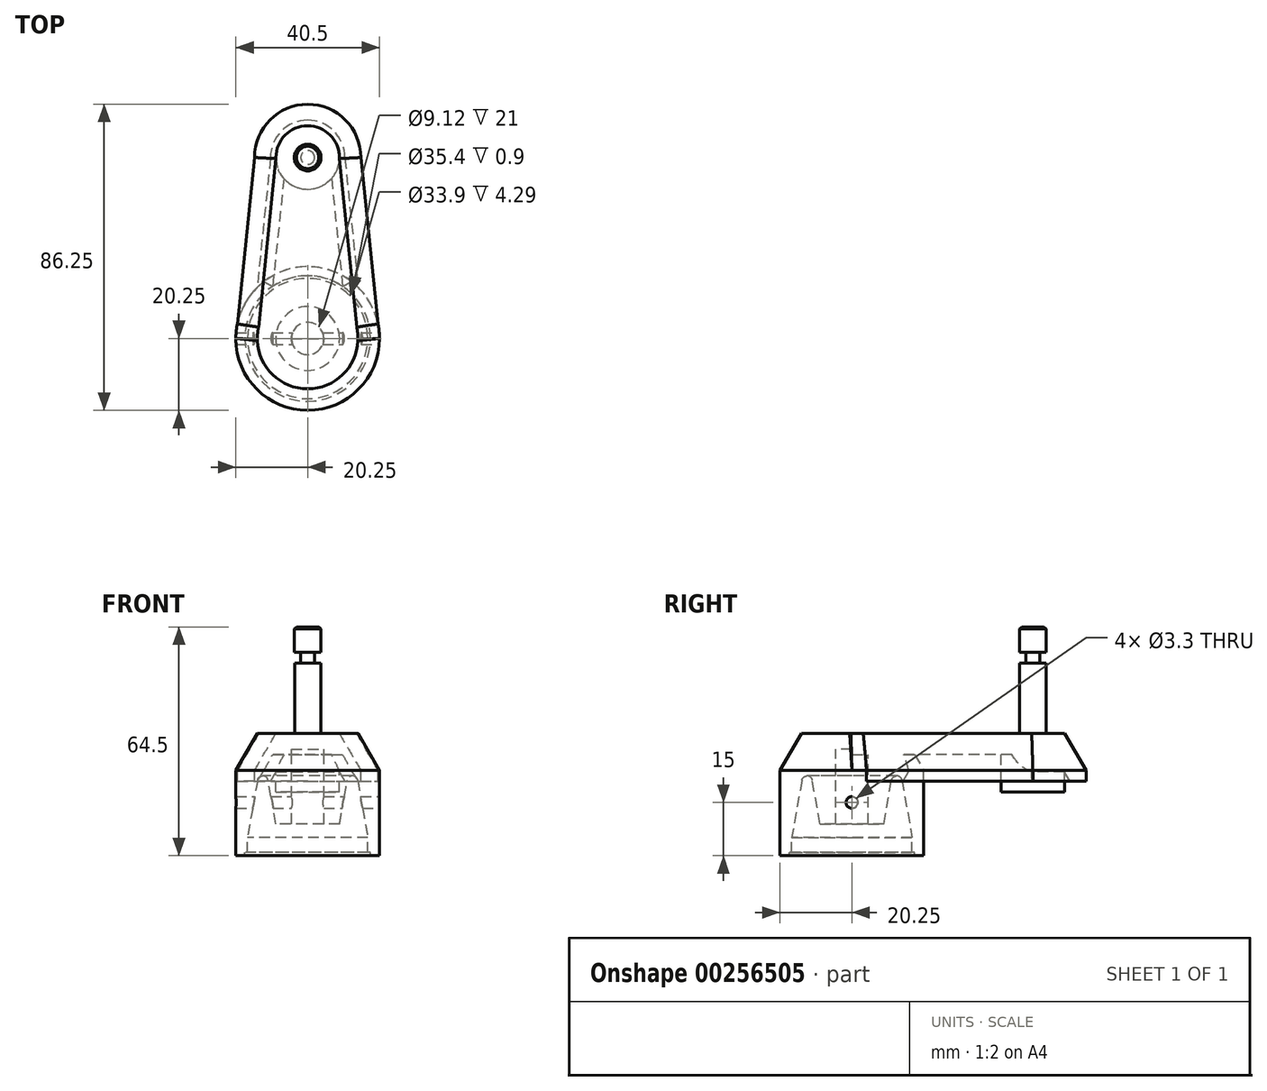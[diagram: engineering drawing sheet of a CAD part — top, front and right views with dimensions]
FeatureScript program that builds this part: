
annotation { "Feature Type Name" : "Feature", "Feature Type Description" : "" }
export const myFeature = defineFeature(function(context is Context, id is Id, definition is map)
    precondition{}
    {
        {
            var Q0;
            Q0=qCreatedBy(makeId("Right.planeOp"),FACE);
            var sketch = newSketch(context, id + "F0", { "sketchPlane" : qUnion([Q0])});
            skPoint(sketch, "E0", {"position": v(0, 11.5) * mm});
            skPoint(sketch, "E1", {"position": v(0, 10) * mm});
            skLineSegment(sketch, "E2", {"start": v(0, 10) * mm, "end": v(-1.52, 10) * mm});
            skLineSegment(sketch, "E3", {"start": v(-1.52, 10) * mm, "end": v(-1.52, 3) * mm});
            skLineSegment(sketch, "E4", {"start": v(-1.52, 3) * mm, "end": v(-3, 3) * mm});
            skLineSegment(sketch, "E5", {"start": v(-3, 3) * mm, "end": v(-3.72, 7.09) * mm});
            skLineSegment(sketch, "E6", {"start": v(-4.7, 7.09) * mm, "end": v(-5.65, 1.73) * mm});
            skLineSegment(sketch, "E7", {"start": v(-5.65, 1.73) * mm, "end": v(-5.65, 0.3) * mm});
            skLineSegment(sketch, "E8", {"start": v(-5.65, 0.3) * mm, "end": v(-5.9, 0.3) * mm});
            skLineSegment(sketch, "E9", {"start": v(-5.9, 0.3) * mm, "end": v(-5.9, 0) * mm});
            skLineSegment(sketch, "E10", {"start": v(-5.9, 0) * mm, "end": v(-6.75, 0) * mm});
            skLineSegment(sketch, "E11", {"start": v(-6.75, 0) * mm, "end": v(-6.75, 8) * mm});
            skLineSegment(sketch, "E12", {"start": v(-6.75, 8) * mm, "end": v(-4.73, 11.5) * mm});
            skLineSegment(sketch, "E13", {"start": v(-4.73, 11.5) * mm, "end": v(0, 11.5) * mm});
            skLineSegment(sketch, "E14", {"start": v(-5.65, 1.73) * mm, "end": v(-5.65, 11.5) * mm, "construction": true});
            skLineSegment(sketch, "E15", {"start": v(-3, 3) * mm, "end": v(-3, 11.5) * mm, "construction": true});
            skPoint(sketch, "E16.visualSharp", {"position": v(-4.21, 9.88) * mm});
            skArc(sketch, "E16.filletArc", {"start": v(-3.72, 7.09) * mm, "mid": v(-4.21, 7.5) * mm, "end": v(-4.7, 7.09) * mm});
            skLineSegment(sketch, "E17", {"start": v(-6.75, 8) * mm, "end": v(-6.75, 11.5) * mm, "construction": true});
            skLineSegment(sketch, "E18", {"start": v(0, 11.5) * mm, "end": v(0, 10) * mm});
            skSolve(sketch);
        }
        {
            var Q0;
            Q0=makeQuery(id+"F0.imprint","IMPRINT",FACE,{"disambiguationData":[TD([[makeQuery(id+"F0.imprint","IMPRINT",EDGE,{"derivedFrom":sQuery(id+"F0.wireOp",EDGE,"E2")}),-1.0]])]});
            var Q1;
            Q1=sQuery(id+"F0.wireOp",EDGE,"E18");
            revolve(context, id + "F1", {"entities" : qUnion([Q0]), "axis" : qUnion([Q1]), "revolveType" : RevolveType.FULL});
        }
        {
            var Q0;
            Q0=qCreatedBy(makeId("Right.planeOp"),FACE);
            var sketch = newSketch(context, id + "F2", { "sketchPlane" : qUnion([Q0])});
            skLineSegment(sketch, "E19", {"start": v(0, 0) * mm, "end": v(17, 0) * mm, "construction": true});
            skLineSegment(sketch, "E20", {"start": v(17, 0) * mm, "end": v(17, 11.5) * mm, "construction": true});
            skPoint(sketch, "E21", {"position": v(17, 9.5) * mm});
            skLineSegment(sketch, "E22", {"start": v(20.5, 7) * mm, "end": v(22, 7) * mm});
            skLineSegment(sketch, "E23", {"start": v(22, 7) * mm, "end": v(22, 8) * mm});
            skLineSegment(sketch, "E24", {"start": v(22, 8) * mm, "end": v(19.98, 11.5) * mm});
            skLineSegment(sketch, "E25", {"start": v(19.98, 11.5) * mm, "end": v(17, 11.5) * mm});
            skLineSegment(sketch, "E26", {"start": v(17, 9.5) * mm, "end": v(17, 11.5) * mm});
            skLineSegment(sketch, "E27", {"start": v(20.5, 7) * mm, "end": v(20.5, 0) * mm, "construction": true});
            skLineSegment(sketch, "E28", {"start": v(20.5, 7) * mm, "end": v(19.06, 9.5) * mm});
            skLineSegment(sketch, "E29", {"start": v(19.06, 9.5) * mm, "end": v(17, 9.5) * mm});
            skSolve(sketch);
        }
        {
            var Q0;
            Q0=qCreatedBy(makeId("Top.planeOp"),FACE);
            cPlane(context, id + "F3", {"entities" : qUnion([Q0]), "cplaneType" : CPlaneType.OFFSET, "offset" : 8 * mm, "width" : 150 * mm, "height" : 150 * mm});
        }
        {
            var Q0;
            Q0=qCreatedBy(id+"F3.planeOp",FACE);
            var sketch = newSketch(context, id + "F4", { "sketchPlane" : qUnion([Q0])});
            skArc(sketch, "E30", {"start": v(5, 17) * mm, "mid": v(3.54, 20.54) * mm, "end": v(0, 22) * mm});
            skPoint(sketch, "E31", {"position": v(0, 0) * mm});
            skLineSegment(sketch, "E32", {"start": v(-5, 17) * mm, "end": v(-6.75, 0) * mm});
            skLineSegment(sketch, "E33", {"start": v(5, 17) * mm, "end": v(6.75, 0) * mm});
            skLineSegment(sketch, "E34", {"start": v(0, 17) * mm, "end": v(0, 22) * mm, "construction": true});
            skLineSegment(sketch, "E35", {"start": v(0, 22) * mm, "end": v(0, 17) * mm, "construction": true});
            skArc(sketch, "E36", {"start": v(0, 22) * mm, "mid": v(-3.54, 20.54) * mm, "end": v(-5, 17) * mm});
            skSolve(sketch);
        }
        {
            var Q0;
            Q0=makeQuery(id+"F2.imprint","IMPRINT",FACE,{"disambiguationData":[TD([[makeQuery(id+"F2.imprint","IMPRINT",EDGE,{"derivedFrom":sQuery(id+"F2.wireOp",EDGE,"E22")}),1.0]])]});
            var Q1;
            Q1=sQuery(id+"F4.wireOp",EDGE,"E30");
            var Q2;
            Q2=sQuery(id+"F4.wireOp",EDGE,"E33");
            sweep(context, id + "F5", {"operationType" : NewBodyOperationType.ADD, "profiles" : qUnion([Q0]), "path" : qUnion([Q1, Q2])});
        }
        {
            var Q0;
            Q0=makeQuery(id+"F2.imprint","IMPRINT",FACE,{"disambiguationData":[TD([[makeQuery(id+"F2.imprint","IMPRINT",EDGE,{"derivedFrom":sQuery(id+"F2.wireOp",EDGE,"E22")}),1.0]])]});
            var Q1;
            Q1=sQuery(id+"F4.wireOp",EDGE,"E36");
            var Q2;
            Q2=sQuery(id+"F4.wireOp",EDGE,"E32");
            sweep(context, id + "F6", {"operationType" : NewBodyOperationType.ADD, "profiles" : qUnion([Q0]), "path" : qUnion([Q1, Q2])});
        }
        {
            var Q0;
            Q0=qCreatedBy(makeId("Front.planeOp"),FACE);
            var sketch = newSketch(context, id + "F7", { "sketchPlane" : qUnion([Q0])});
            skLineSegment(sketch, "E37.bottom", {"start": v(-2.5, 11.5) * mm, "end": v(2.5, 11.5) * mm});
            skLineSegment(sketch, "E37.top", {"start": v(-2.5, 9.5) * mm, "end": v(2.5, 9.5) * mm});
            skLineSegment(sketch, "E37.left", {"start": v(-2.5, 11.5) * mm, "end": v(-2.5, 9.5) * mm});
            skLineSegment(sketch, "E37.right", {"start": v(2.5, 11.5) * mm, "end": v(2.5, 9.5) * mm});
            skSolve(sketch);
        }
        {
            var Q0;
            Q0=makeQuery(id+"F7.imprint","IMPRINT",FACE,{"disambiguationData":[TD([[makeQuery(id+"F7.imprint","IMPRINT",EDGE,{"derivedFrom":sQuery(id+"F7.wireOp",EDGE,"E37.bottom")}),-1.0]])]});
            extrude(context, id + "F8", {"entities" : qUnion([Q0]), "operationType" : NewBodyOperationType.ADD, "oppositeDirection" : true, "depth" : 17 * mm});
        }
        {
            var Q0;
            {var subQ0=sQuery(id+"F2.wireOp",EDGE,"E25");Q0=makeQuery(id+"F8.boolean.opBoolean","MERGE",FACE,{"derivedFrom":[makeQuery(id+"F6.boolean.opBoolean","MERGE",FACE,{"derivedFrom":[makeQuery(id+"F5.boolean.opBoolean","MERGE",FACE,{"derivedFrom":[makeQuery(id+"F1.opRevolve","SWEPT_FACE",FACE,{"disambiguationData":[OSD([sQuery(id+"F0.wireOp",EDGE,"E13")])]}),makeQuery(id+"F5.opSweep","MID_CAP_FACE",FACE,{"disambiguationData":[OSD([subQ0,sQuery(id+"F4.wireOp",VERTEX,"E33.start")])],"capPos":1.0})]}),makeQuery(id+"F6.opSweep","MID_CAP_FACE",FACE,{"disambiguationData":[OSD([subQ0,sQuery(id+"F4.wireOp",VERTEX,"E32.start")])],"capPos":1.0})]}),makeQuery(id+"F8.opExtrude","SWEPT_FACE",FACE,{"disambiguationData":[OSD([sQuery(id+"F7.wireOp",EDGE,"E37.bottom")])]})]});}
            var sketch = newSketch(context, id + "F9", { "sketchPlane" : qUnion([Q0])});
            skLineSegment(sketch, "E38", {"start": v(0, 0) * mm, "end": v(0, 17) * mm, "construction": true});
            skCircle(sketch, "E39", {"center": v(0, 17) * mm, "radius": 2.98 * mm});
            skCircle(sketch, "E40", {"center": v(0, 17) * mm, "radius": 1.23 * mm});
            skSolve(sketch);
        }
        {
            var Q0;
            {var subQ0=sQuery(id+"F2.wireOp",EDGE,"E24");var subQ1=sQuery(id+"F2.wireOp",EDGE,"E25");var subQ2=sQuery(id+"F4.wireOp",EDGE,"E36");var subQ3=makeQuery(id+"F6.opSweep","SWEPT_EDGE",EDGE,{"disambiguationData":[OSD([subQ0,subQ1,subQ2]),OD(1.0)]});var subQ4=makeQuery(id+"F9.imprint","IMPRINT",EDGE,{"derivedFrom":subQ3});var subQ12=sQuery(id+"F4.wireOp",EDGE,"E30");var subQ13=makeQuery(id+"F5.opSweep","SWEPT_EDGE",EDGE,{"disambiguationData":[OSD([subQ0,subQ1,subQ12]),OD(1.0)]});var subQ14=makeQuery(id+"F9.imprint","IMPRINT",EDGE,{"derivedFrom":subQ13});Q0=qUnion([makeQuery(id+"F9.imprint","IMPRINT",FACE,{"disambiguationData":[TD([[subQ4,-1.0]])]}),makeQuery(id+"F9.imprint","IMPRINT",FACE,{"disambiguationData":[TD([[subQ14,1.0]])]}),makeQuery(id+"F9.imprint","IMPRINT",FACE,{"disambiguationData":[TD([[makeQuery(id+"F9.imprint","IMPRINT",EDGE,{"derivedFrom":sQuery(id+"F9.wireOp",EDGE,"E40")}),-1.0]])]})]);}
            var Q1;
            Q1=makeQuery(id+"F9.imprint","IMPRINT",FACE,{"disambiguationData":[TD([[makeQuery(id+"F9.imprint","IMPRINT",EDGE,{"derivedFrom":sQuery(id+"F9.wireOp",EDGE,"E40")}),1.0]])]});
            extrude(context, id + "F10", {"entities" : qUnion([Q0, Q1]), "operationType" : NewBodyOperationType.ADD, "oppositeDirection" : true, "depth" : 5.5 * mm});
        }
        {
            var Q0;
            Q0=makeQuery(id+"F9.imprint","IMPRINT",FACE,{"disambiguationData":[TD([[makeQuery(id+"F9.imprint","IMPRINT",EDGE,{"derivedFrom":sQuery(id+"F9.wireOp",EDGE,"E40")}),1.0]])]});
            extrude(context, id + "F11", {"entities" : qUnion([Q0]), "operationType" : NewBodyOperationType.ADD, "depth" : 6.6 * mm});
        }
        {
            var Q0;
            Q0=makeQuery(id+"F11.opExtrude","CAP_FACE",FACE,{"disambiguationData":[OSD([sQuery(id+"F9.wireOp",EDGE,"E40")])],"isStart":false});
            var sketch = newSketch(context, id + "F12", { "sketchPlane" : qUnion([Q0])});
            skCircle(sketch, "E41", {"center": v(0, 17) * mm, "radius": 0.65 * mm});
            skSolve(sketch);
        }
        {
            var Q0;
            Q0=makeQuery(id+"F12.imprint","IMPRINT",FACE,{"disambiguationData":[TD([[makeQuery(id+"F12.imprint","IMPRINT",EDGE,{"derivedFrom":sQuery(id+"F12.wireOp",EDGE,"E41")}),1.0]])]});
            extrude(context, id + "F13", {"entities" : qUnion([Q0]), "operationType" : NewBodyOperationType.ADD, "depth" : 1 * mm});
        }
        {
            var Q0;
            Q0=makeQuery(id+"F13.opExtrude","CAP_FACE",FACE,{"disambiguationData":[OSD([sQuery(id+"F12.wireOp",EDGE,"E41")])],"isStart":false});
            var sketch = newSketch(context, id + "F14", { "sketchPlane" : qUnion([Q0])});
            skCircle(sketch, "E42", {"center": v(0, 17) * mm, "radius": 1.25 * mm});
            skSolve(sketch);
        }
        {
            var Q0;
            {var subQ0=makeQuery(id+"F14.imprint","IMPRINT",EDGE,{"derivedFrom":makeQuery(id+"F13.opExtrude","CAP_EDGE",EDGE,{"disambiguationData":[OSD([sQuery(id+"F12.wireOp",EDGE,"E41")])],"isStart":false})});Q0=qUnion([makeQuery(id+"F14.imprint","IMPRINT",FACE,{"disambiguationData":[TD([[makeQuery(id+"F14.imprint","IMPRINT",EDGE,{"derivedFrom":sQuery(id+"F14.wireOp",EDGE,"E42")}),1.0]])]}),makeQuery(id+"F14.imprint","IMPRINT",FACE,{"disambiguationData":[TD([[subQ0,1.0]])]})]);}
            extrude(context, id + "F15", {"entities" : qUnion([Q0]), "operationType" : NewBodyOperationType.ADD, "depth" : 2.4 * mm});
        }
        {
            var Q0;
            Q0=makeQuery(id+"F15.opExtrude","CAP_EDGE",EDGE,{"disambiguationData":[OSD([sQuery(id+"F14.wireOp",EDGE,"E42")])],"isStart":false});
            chamfer(context, id + "F16", {"entities" : qUnion([Q0]), "width" : 0.2 * mm, "tangentPropagation" : true});
        }
        {
            var Q0;
            Q0=makeQuery(id+"F1.opRevolve","SWEPT_BODY",BODY,{"disambiguationData":[OSD([sQuery(id+"F0.wireOp",EDGE,"E2"),sQuery(id+"F0.wireOp",EDGE,"E3"),sQuery(id+"F0.wireOp",EDGE,"E4"),sQuery(id+"F0.wireOp",EDGE,"E5"),sQuery(id+"F0.wireOp",EDGE,"E6"),sQuery(id+"F0.wireOp",EDGE,"E7"),sQuery(id+"F0.wireOp",EDGE,"E8"),sQuery(id+"F0.wireOp",EDGE,"E9"),sQuery(id+"F0.wireOp",EDGE,"E10"),sQuery(id+"F0.wireOp",EDGE,"E11"),sQuery(id+"F0.wireOp",EDGE,"E12"),sQuery(id+"F0.wireOp",EDGE,"E13"),sQuery(id+"F0.wireOp",EDGE,"E16.filletArc"),sQuery(id+"F0.wireOp",EDGE,"E18")])]});
            var Q1;
            Q1=qCreatedBy(makeId("Origin.pointOp"),VERTEX);
            transform(context, id + "F17", {"entities" : qUnion([Q0]), "transformType" : TransformType.SCALE_UNIFORMLY, "scale" : 3, "makeCopy" : false, "scalePoint" : qUnion([Q1])});
        }
        {
            var Q0;
            Q0=qCreatedBy(makeId("Right.planeOp"),FACE);
            var sketch = newSketch(context, id + "F18", { "sketchPlane" : qUnion([Q0])});
            skCircle(sketch, "E43", {"center": v(0, 15) * mm, "radius": 1.65 * mm});
            skSolve(sketch);
        }
        {
            var Q0;
            Q0=qSketchRegion(id+"F18",true);
            extrude(context, id + "F19", {"entities" : qUnion([Q0]), "operationType" : NewBodyOperationType.REMOVE, "oppositeDirection" : true, "depth" : 42 * mm, "symmetric" : true});
        }
    });
